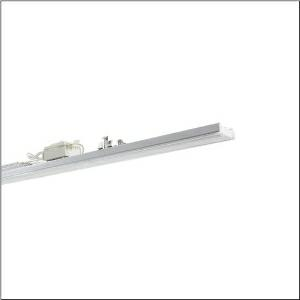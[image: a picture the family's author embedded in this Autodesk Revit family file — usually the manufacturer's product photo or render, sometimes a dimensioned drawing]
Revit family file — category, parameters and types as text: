
# Revit family: licross_r__21_recessed_mo_52te18cn49xg_07a5
name_source: partatom
category: Lighting Fixtures
units: mm (PartAtom-declared; Revit-internal decimal feet)

## family parameters
Cut with Voids When Loaded = No
Host = Face
Light Source = No
Part Type = Normal
Room Calculation Point = No
Round Connector Dimension = Use Diameter
Shared = No

## types (1)
- --- (1 x LED, 9000 lm, 49.9 W, 4000K)
    Apparent Load = 50 VA
    CIE Flux Codes = 79 95 99 100 100
    Color Rendering = 80
    Color Temperature = 4000K
    Default Elevation = 1800 mm
    Description = Licross® 21 Recessed MO, luminaire insert, of sheet steel, galvanised, coil coated, white, length: 1.500mm, width: 66mm, height: 67mm, LED rated luminous flux: 9.000lm, light colour: 840, control gear: ON/OFF Multilumen, CLOi, control gear: ECG Multilumen, with plug, 3-pole, with phase selection, mains connection: 220..240V, AC, 50/60Hz, start of lifetime: 50W, end of service life: 61W, halogen-free wiring, primary light control with lens, of plastic, primary optical cover: cover, of PMMA, light emission: direct distribution, primary light characteristic: symmetric, protection rating (complete): IP54, insulation class (complete): insulation class I (protective earthing), certification: CE, ENEC, VDE, UKCA, protection symbol: D if used in an environment with non-conductive dust loads with corresponding accessories, impact resistance: IK06, permissible ambient temperature for indoor applications: -35..+40°C, corresponds to IFS (International Featured Standards) requirements for safety and quality in the food industry, reducing of maximum allowable ambient temperature of 5°C with ceiling mounting, LABS conformity tested according to VDMA 24364:2018-05, packaging unit: 1 piece
    Height = 58 mm
    Lamp = 1 x LED
    Lamp Light Flux = 9000 lm
    Lamp Power = 49.9 W
    Lamp count = 1
    Length = 1500 mm
    Luminous efficacy = 180 lm/W
    Manufacturer = Siteco
    ModVariant = No
    Model = 52TE18CN49XG
    Mounting Place = Ceiling
    Mounting Type = Pendant
    Number of Poles = 1
    OnlyDefault = Yes
    Power Factor = 1
    Product Name = Licross® 21 Recessed MO
    Product group = luminaire insert
    ProductGroupID = 902
    Protection Class = Protection class I
    Protection Degree = IP 54
    RLX_Detail_Level = 1
    RLX_Emergency_Light_Flux = 0 lm
    RLX_Emergency_Type = 0
    RLX_Emergency_Type_DB = No
    RlxData = <blob elided: 22329 chars, md5=40ee6efb>
    Socket = socket
    Standby Power = 0 W
    System Light Flux = 9000 lm
    System Power = 50 W
    Type Comments = factory setting: luminous flux: 100 % | (A | C | E) | 116 mA
    Type Image = l_1296930.jpg
    URL = http://relux.com
    VarID = @adj_110018
    Voltage = 0 V
    Weight = 0.00 kg
    Width = 66 mm

## geometry (parser evidence)
native form markers: Blend x4, Sweep x10
no freeform markers — native parametric forms only
